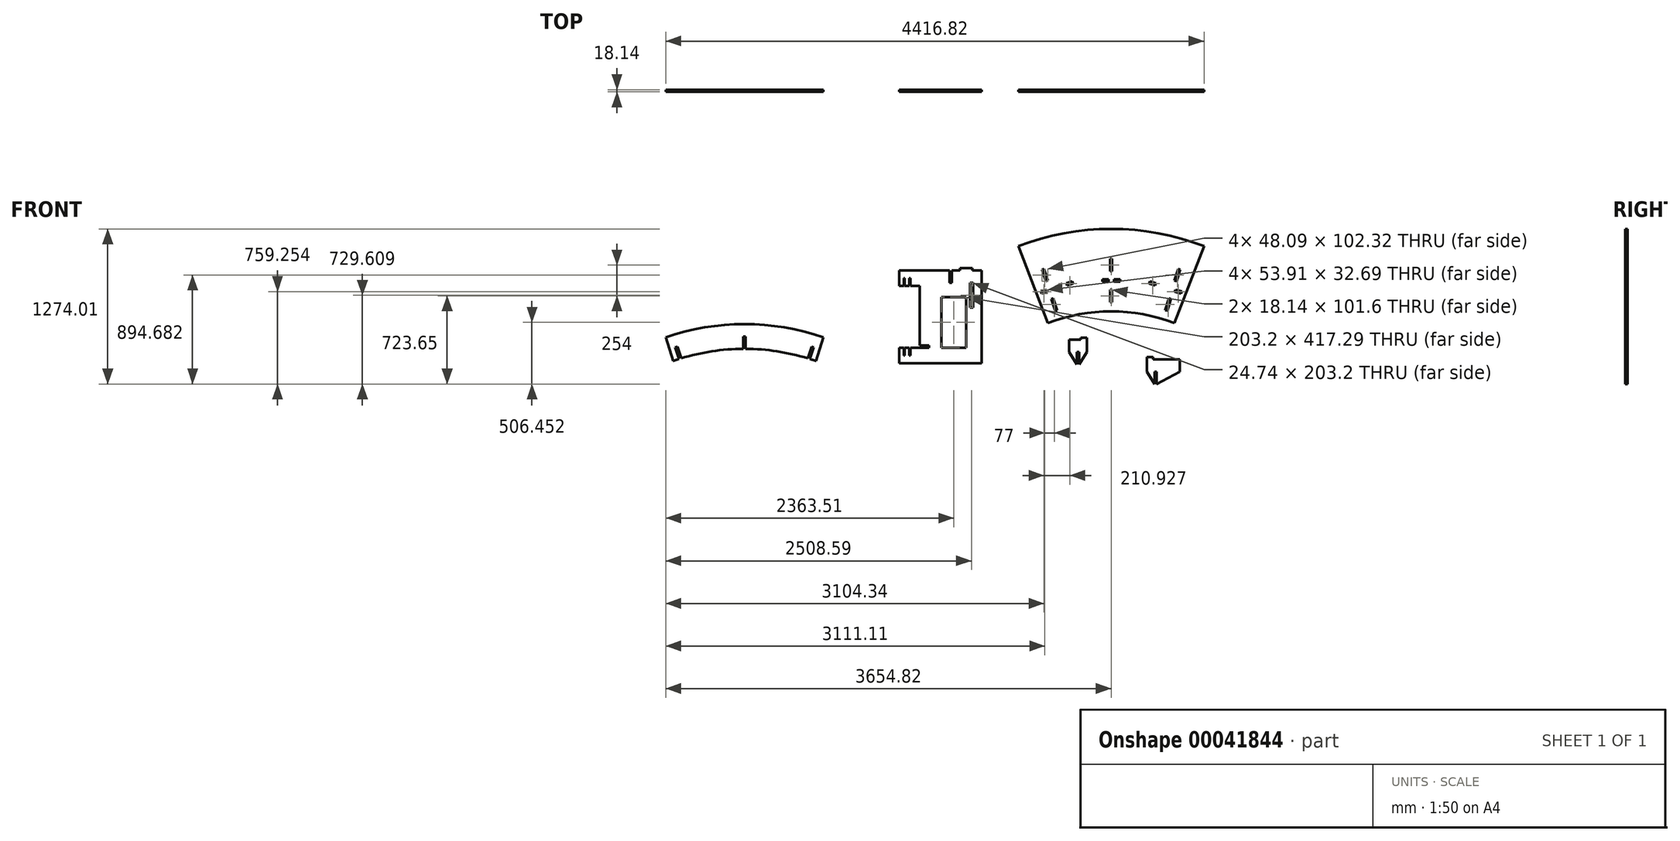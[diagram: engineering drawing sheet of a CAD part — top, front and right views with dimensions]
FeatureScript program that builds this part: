
annotation { "Feature Type Name" : "Feature", "Feature Type Description" : "" }
export const myFeature = defineFeature(function(context is Context, id is Id, definition is map)
    precondition{}
    {
        {
            var Q0;
            Q0=qCreatedBy(makeId("Front.planeOp"),FACE);
            var sketch = newSketch(context, id + "F0", { "sketchPlane" : qUnion([Q0])});
            skArc(sketch, "E0", {"start": v(822.71, 0) * mm, "mid": v(60.71, 141.8) * mm, "end": v(-701.29, 0) * mm});
            skArc(sketch, "E1.0", {"start": v(579.07, -632) * mm, "mid": v(60.71, -535.54) * mm, "end": v(-457.65, -632) * mm});
            skLineSegment(sketch, "E2", {"start": v(-701.29, 0) * mm, "end": v(-457.65, -632) * mm});
            skLineSegment(sketch, "E3", {"start": v(579.07, -632) * mm, "end": v(822.71, 0) * mm});
            skLineSegment(sketch, "E4.bottom", {"start": v(-1510, -199.4) * mm, "end": v(-1002, -199.4) * mm});
            skLineSegment(sketch, "E4.top", {"start": v(-1510, -961.4) * mm, "end": v(-1002, -961.4) * mm});
            skLineSegment(sketch, "E4.left", {"start": v(-1510, -326.4) * mm, "end": v(-1510, -815.86) * mm});
            skLineSegment(sketch, "E4.right", {"start": v(-1002, -199.4) * mm, "end": v(-1002, -961.4) * mm});
            skLineSegment(sketch, "E5.bottom", {"start": v(-1510, -199.4) * mm, "end": v(-1679.33, -199.4) * mm});
            skLineSegment(sketch, "E5.top", {"start": v(-1510, -326.4) * mm, "end": v(-1585.35, -326.4) * mm});
            skLineSegment(sketch, "E5.right", {"start": v(-1679.33, -199.4) * mm, "end": v(-1679.33, -326.4) * mm});
            skLineSegment(sketch, "E6", {"start": v(-1510, -580.4) * mm, "end": v(-1002, -580.4) * mm, "construction": true});
            skLineSegment(sketch, "E7", {"start": v(-1679.33, -262.9) * mm, "end": v(-1641.23, -262.9) * mm, "construction": true});
            skLineSegment(sketch, "E8.top", {"start": v(-1641.23, -262.9) * mm, "end": v(-1632.34, -262.9) * mm});
            skLineSegment(sketch, "E8.left", {"start": v(-1641.23, -326.4) * mm, "end": v(-1641.23, -262.9) * mm});
            skLineSegment(sketch, "E8.right", {"start": v(-1632.34, -326.4) * mm, "end": v(-1632.34, -262.9) * mm});
            skLineSegment(sketch, "E9", {"start": v(-1632.34, -262.9) * mm, "end": v(-1594.24, -262.9) * mm, "construction": true});
            skLineSegment(sketch, "E10.top", {"start": v(-1594.24, -262.9) * mm, "end": v(-1585.35, -262.9) * mm});
            skLineSegment(sketch, "E10.left", {"start": v(-1594.24, -326.4) * mm, "end": v(-1594.24, -262.9) * mm});
            skLineSegment(sketch, "E10.right", {"start": v(-1585.35, -326.4) * mm, "end": v(-1585.35, -262.9) * mm});
            skLineSegment(sketch, "E11.trimOffspring", {"start": v(-1641.23, -326.4) * mm, "end": v(-1679.33, -326.4) * mm});
            skLineSegment(sketch, "E12.trimOffspring", {"start": v(-1594.24, -326.4) * mm, "end": v(-1632.34, -326.4) * mm});
            skLineSegment(sketch, "E13.MirrorCS", {"start": v(-1641.23, -834.4) * mm, "end": v(-1679.33, -834.4) * mm});
            skLineSegment(sketch, "E14.MirrorCS", {"start": v(-1510, -834.4) * mm, "end": v(-1585.35, -834.4) * mm});
            skLineSegment(sketch, "E15.MirrorCS", {"start": v(-1632.34, -897.9) * mm, "end": v(-1594.24, -897.9) * mm, "construction": true});
            skLineSegment(sketch, "E16.MirrorCS", {"start": v(-1679.33, -897.9) * mm, "end": v(-1641.23, -897.9) * mm, "construction": true});
            skLineSegment(sketch, "E17.MirrorCS", {"start": v(-1594.24, -834.4) * mm, "end": v(-1594.24, -897.9) * mm});
            skLineSegment(sketch, "E18.MirrorCS", {"start": v(-1594.24, -834.4) * mm, "end": v(-1632.34, -834.4) * mm});
            skLineSegment(sketch, "E19.MirrorCS", {"start": v(-1679.33, -961.4) * mm, "end": v(-1679.33, -834.4) * mm});
            skLineSegment(sketch, "E20.MirrorCS", {"start": v(-1632.34, -834.4) * mm, "end": v(-1632.34, -897.9) * mm});
            skLineSegment(sketch, "E21.MirrorCS", {"start": v(-1641.23, -834.4) * mm, "end": v(-1641.23, -897.9) * mm});
            skLineSegment(sketch, "E22.MirrorCS", {"start": v(-1510, -961.4) * mm, "end": v(-1679.33, -961.4) * mm});
            skLineSegment(sketch, "E23.MirrorCS", {"start": v(-1641.23, -897.9) * mm, "end": v(-1632.34, -897.9) * mm});
            skLineSegment(sketch, "E24.MirrorCS", {"start": v(-1594.24, -897.9) * mm, "end": v(-1585.35, -897.9) * mm});
            skLineSegment(sketch, "E25.MirrorCS", {"start": v(-1585.35, -834.4) * mm, "end": v(-1585.35, -897.9) * mm});
            skLineSegment(sketch, "E26", {"start": v(-376.14, -603.35) * mm, "end": v(-581.47, 42.11) * mm, "construction": true});
            skLineSegment(sketch, "E27", {"start": v(60.71, -1976.58) * mm, "end": v(60.71, 636.15) * mm, "construction": true});
            skLineSegment(sketch, "E28", {"start": v(-476.24, -288.69) * mm, "end": v(-458.95, -283.19) * mm});
            skLineSegment(sketch, "E29", {"start": v(-458.95, -283.19) * mm, "end": v(-489.75, -186.37) * mm});
            skLineSegment(sketch, "E30", {"start": v(-489.75, -186.37) * mm, "end": v(-507.04, -191.87) * mm});
            skLineSegment(sketch, "E31", {"start": v(-507.04, -191.87) * mm, "end": v(-476.24, -288.69) * mm});
            skLineSegment(sketch, "E32.bottom", {"start": v(-1433.8, -199.4) * mm, "end": v(-1332.2, -199.4) * mm});
            skLineSegment(sketch, "E32.top", {"start": v(-1433.8, -181.26) * mm, "end": v(-1332.2, -181.26) * mm});
            skLineSegment(sketch, "E32.left", {"start": v(-1433.8, -199.4) * mm, "end": v(-1433.8, -181.26) * mm});
            skLineSegment(sketch, "E32.right", {"start": v(-1332.2, -199.4) * mm, "end": v(-1332.2, -181.26) * mm});
            skLineSegment(sketch, "E33", {"start": v(-1256, -199.4) * mm, "end": v(-1256, -961.4) * mm, "construction": true});
            skLineSegment(sketch, "E34.MirrorCS", {"start": v(-1078.2, -199.4) * mm, "end": v(-1078.2, -181.26) * mm});
            skLineSegment(sketch, "E35.MirrorCS", {"start": v(-1078.2, -199.4) * mm, "end": v(-1179.8, -199.4) * mm});
            skLineSegment(sketch, "E36.MirrorCS", {"start": v(-1179.8, -199.4) * mm, "end": v(-1179.8, -181.26) * mm});
            skLineSegment(sketch, "E37.MirrorCS", {"start": v(-1078.2, -181.26) * mm, "end": v(-1179.8, -181.26) * mm});
            skLineSegment(sketch, "E38.bottom", {"start": v(51.64, -103.76) * mm, "end": v(69.78, -103.76) * mm});
            skLineSegment(sketch, "E38.top", {"start": v(51.64, -205.36) * mm, "end": v(69.78, -205.36) * mm});
            skLineSegment(sketch, "E38.left", {"start": v(51.64, -103.76) * mm, "end": v(51.64, -205.36) * mm});
            skLineSegment(sketch, "E38.right", {"start": v(69.78, -103.76) * mm, "end": v(69.78, -205.36) * mm});
            skPoint(sketch, "E39", {"position": v(60.71, -103.76) * mm});
            skLineSegment(sketch, "E40", {"start": v(51.71, -281.56) * mm, "end": v(78.37, -281.56) * mm, "construction": true});
            skPoint(sketch, "E41.MirrorP", {"position": v(60.71, -459.36) * mm});
            skLineSegment(sketch, "E42.MirrorCS", {"start": v(51.64, -459.36) * mm, "end": v(69.78, -459.36) * mm});
            skLineSegment(sketch, "E43.MirrorCS", {"start": v(51.64, -459.36) * mm, "end": v(51.64, -357.76) * mm});
            skLineSegment(sketch, "E44.MirrorCS", {"start": v(51.64, -357.76) * mm, "end": v(69.78, -357.76) * mm});
            skLineSegment(sketch, "E45.MirrorCS", {"start": v(69.78, -459.36) * mm, "end": v(69.78, -357.76) * mm});
            skPoint(sketch, "E46", {"position": v(61.08, -535.54) * mm});
            skPoint(sketch, "E47", {"position": v(61.08, 141.8) * mm});
            skLineSegment(sketch, "E48.bottom", {"start": v(-283.81, -768.8) * mm, "end": v(-138.67, -768.8) * mm});
            skLineSegment(sketch, "E48.left", {"start": v(-283.81, -768.8) * mm, "end": v(-283.81, -870.4) * mm});
            skLineSegment(sketch, "E49.left", {"start": v(-220.31, -870.4) * mm, "end": v(-220.31, -972) * mm});
            skLineSegment(sketch, "E49.right", {"start": v(-202.17, -870.4) * mm, "end": v(-202.17, -972) * mm});
            skPoint(sketch, "E50", {"position": v(-211.24, -870.4) * mm});
            skLineSegment(sketch, "E49.bottom", {"start": v(-220.31, -870.4) * mm, "end": v(-202.17, -870.4) * mm});
            skLineSegment(sketch, "E51", {"start": v(-283.81, -870.4) * mm, "end": v(-220.31, -972) * mm});
            skLineSegment(sketch, "E52.left", {"start": v(-1265.07, -199.4) * mm, "end": v(-1265.07, -301) * mm});
            skPoint(sketch, "E53", {"position": v(-1256, -301) * mm});
            skLineSegment(sketch, "E52.right", {"start": v(-1246.92, -199.4) * mm, "end": v(-1246.92, -301) * mm});
            skPoint(sketch, "E54", {"position": v(-1256, -199.4) * mm});
            skLineSegment(sketch, "E52.bottom", {"start": v(-1265.07, -199.4) * mm, "end": v(-1246.92, -199.4) * mm});
            skLineSegment(sketch, "E52.top", {"start": v(-1265.07, -301) * mm, "end": v(-1246.92, -301) * mm});
            skPoint(sketch, "E55.orphan", {"position": v(-283.81, -972) * mm});
            skPoint(sketch, "E56.orphan", {"position": v(-84.24, -972) * mm});
            skLineSegment(sketch, "E57", {"start": v(-211.24, -870.4) * mm, "end": v(-211.24, -744.65) * mm, "construction": true});
            skLineSegment(sketch, "E58.MirrorCS", {"start": v(-138.67, -768.8) * mm, "end": v(-138.67, -870.4) * mm});
            skLineSegment(sketch, "E59.MirrorCS", {"start": v(-138.67, -870.4) * mm, "end": v(-202.17, -972) * mm});
            skLineSegment(sketch, "E60.bottom", {"start": v(-283.81, -768.8) * mm, "end": v(-233.01, -768.8) * mm});
            skLineSegment(sketch, "E60.top", {"start": v(-283.81, -750.67) * mm, "end": v(-233.01, -750.67) * mm});
            skLineSegment(sketch, "E60.left", {"start": v(-283.81, -768.8) * mm, "end": v(-283.81, -750.67) * mm});
            skLineSegment(sketch, "E60.right", {"start": v(-233.01, -768.8) * mm, "end": v(-233.01, -750.67) * mm});
            skLineSegment(sketch, "E61.MirrorCS", {"start": v(-189.47, -768.8) * mm, "end": v(-189.47, -750.67) * mm});
            skLineSegment(sketch, "E62.MirrorCS", {"start": v(-138.67, -768.8) * mm, "end": v(-138.67, -750.67) * mm});
            skLineSegment(sketch, "E63.MirrorCS", {"start": v(-138.67, -768.8) * mm, "end": v(-189.47, -768.8) * mm});
            skLineSegment(sketch, "E64.MirrorCS", {"start": v(-138.67, -750.67) * mm, "end": v(-189.47, -750.67) * mm});
            skLineSegment(sketch, "E65", {"start": v(-516.73, -372.01) * mm, "end": v(-511.23, -389.3) * mm});
            skPoint(sketch, "E66.positionSnap0", {"position": v(-513.98, -380.66) * mm});
            skLineSegment(sketch, "E67", {"start": v(-516.73, -372.01) * mm, "end": v(-468.32, -356.61) * mm});
            skLineSegment(sketch, "E68", {"start": v(-511.23, -389.3) * mm, "end": v(-462.82, -373.9) * mm});
            skLineSegment(sketch, "E69", {"start": v(-468.32, -356.61) * mm, "end": v(-462.82, -373.9) * mm});
            skPoint(sketch, "E70", {"position": v(60.79, -132.27) * mm});
            skLineSegment(sketch, "E71", {"start": v(-233.01, -759.74) * mm, "end": v(-189.47, -759.74) * mm, "construction": true});
            skPoint(sketch, "E72", {"position": v(-211.24, -759.74) * mm});
            skLineSegment(sketch, "E73.left", {"start": v(-11.86, -290.63) * mm, "end": v(-11.86, -272.49) * mm});
            skLineSegment(sketch, "E73.bottom", {"start": v(-11.86, -290.63) * mm, "end": v(38.94, -290.63) * mm});
            skLineSegment(sketch, "E73.top", {"start": v(-11.86, -272.49) * mm, "end": v(38.94, -272.49) * mm});
            skLineSegment(sketch, "E73.right", {"start": v(38.94, -290.63) * mm, "end": v(38.94, -272.49) * mm});
            skLineSegment(sketch, "E74.MirrorCS", {"start": v(133.28, -290.63) * mm, "end": v(133.28, -272.49) * mm});
            skLineSegment(sketch, "E75.MirrorCS", {"start": v(133.28, -290.63) * mm, "end": v(82.48, -290.63) * mm});
            skLineSegment(sketch, "E76.MirrorCS", {"start": v(82.48, -290.63) * mm, "end": v(82.48, -272.49) * mm});
            skLineSegment(sketch, "E77.MirrorCS", {"start": v(133.28, -272.49) * mm, "end": v(82.48, -272.49) * mm});
            skPoint(sketch, "E78", {"position": v(38.94, -281.56) * mm});
            skLineSegment(sketch, "E79", {"start": v(38.94, -281.56) * mm, "end": v(51.71, -281.56) * mm, "construction": true});
            skLineSegment(sketch, "E80", {"start": v(-465.57, -365.26) * mm, "end": v(-303.05, -313.56) * mm, "construction": true});
            skLineSegment(sketch, "E81.MirrorCS", {"start": v(-430.04, -433.92) * mm, "end": v(-412.75, -428.42) * mm});
            skLineSegment(sketch, "E82.MirrorCS", {"start": v(-381.95, -525.24) * mm, "end": v(-399.24, -530.74) * mm});
            skLineSegment(sketch, "E83.MirrorCS", {"start": v(-399.24, -530.74) * mm, "end": v(-430.04, -433.92) * mm});
            skLineSegment(sketch, "E84.MirrorCS", {"start": v(-412.75, -428.42) * mm, "end": v(-381.95, -525.24) * mm});
            skLineSegment(sketch, "E85.MirrorCS", {"start": v(597.66, -288.69) * mm, "end": v(580.37, -283.19) * mm});
            skLineSegment(sketch, "E86.MirrorCS", {"start": v(611.17, -186.37) * mm, "end": v(628.46, -191.87) * mm});
            skLineSegment(sketch, "E87.MirrorCS", {"start": v(580.37, -283.19) * mm, "end": v(611.17, -186.37) * mm});
            skLineSegment(sketch, "E88.MirrorCS", {"start": v(628.46, -191.87) * mm, "end": v(597.66, -288.69) * mm});
            skLineSegment(sketch, "E89.MirrorCS", {"start": v(551.46, -433.92) * mm, "end": v(534.17, -428.42) * mm});
            skLineSegment(sketch, "E90.MirrorCS", {"start": v(503.37, -525.24) * mm, "end": v(520.66, -530.74) * mm});
            skLineSegment(sketch, "E91.MirrorCS", {"start": v(520.66, -530.74) * mm, "end": v(551.46, -433.92) * mm});
            skLineSegment(sketch, "E92.MirrorCS", {"start": v(534.17, -428.42) * mm, "end": v(503.37, -525.24) * mm});
            skLineSegment(sketch, "E93.MirrorCS", {"start": v(638.15, -372.01) * mm, "end": v(632.65, -389.3) * mm});
            skLineSegment(sketch, "E94.MirrorCS", {"start": v(589.74, -356.61) * mm, "end": v(584.24, -373.9) * mm});
            skPoint(sketch, "E95.MirrorP", {"position": v(635.4, -380.66) * mm});
            skLineSegment(sketch, "E96.MirrorCS", {"start": v(632.65, -389.3) * mm, "end": v(584.24, -373.9) * mm});
            skLineSegment(sketch, "E97.MirrorCS", {"start": v(638.15, -372.01) * mm, "end": v(589.74, -356.61) * mm});
            skLineSegment(sketch, "E98", {"start": v(-384.31, -339.4) * mm, "end": v(-444.42, -150.46) * mm, "construction": true});
            skPoint(sketch, "E99.MirrorP", {"position": v(-254.64, -298.16) * mm});
            skLineSegment(sketch, "E100.MirrorCS", {"start": v(-305.8, -304.91) * mm, "end": v(-300.3, -322.2) * mm});
            skLineSegment(sketch, "E101.MirrorCS", {"start": v(-257.4, -289.51) * mm, "end": v(-251.9, -306.8) * mm});
            skLineSegment(sketch, "E102.MirrorCS", {"start": v(-257.4, -289.51) * mm, "end": v(-305.8, -304.91) * mm});
            skLineSegment(sketch, "E103.MirrorCS", {"start": v(-251.9, -306.8) * mm, "end": v(-300.3, -322.2) * mm});
            skLineSegment(sketch, "E104.MirrorCS", {"start": v(378.81, -289.51) * mm, "end": v(373.31, -306.8) * mm});
            skPoint(sketch, "E105.MirrorP", {"position": v(376.06, -298.16) * mm});
            skLineSegment(sketch, "E106.MirrorCS", {"start": v(373.31, -306.8) * mm, "end": v(421.72, -322.2) * mm});
            skLineSegment(sketch, "E107.MirrorCS", {"start": v(427.22, -304.91) * mm, "end": v(421.72, -322.2) * mm});
            skLineSegment(sketch, "E108.MirrorCS", {"start": v(378.81, -289.51) * mm, "end": v(427.22, -304.91) * mm});
            skLineSegment(sketch, "E109", {"start": v(-1299.86, -199.4) * mm, "end": v(-1299.86, -417.12) * mm, "construction": true});
            skLineSegment(sketch, "E110", {"start": v(-1002, -510.07) * mm, "end": v(-1129, -510.07) * mm, "construction": true});
            skLineSegment(sketch, "E111", {"start": v(-1319.66, -961.4) * mm, "end": v(-1319.66, -834.4) * mm, "construction": true});
            skLineSegment(sketch, "E112.bottom", {"start": v(-1332.2, -417.12) * mm, "end": v(-1129, -417.12) * mm});
            skLineSegment(sketch, "E112.top", {"start": v(-1332.2, -834.4) * mm, "end": v(-1129, -834.4) * mm});
            skLineSegment(sketch, "E112.left", {"start": v(-1332.2, -417.12) * mm, "end": v(-1332.2, -834.4) * mm});
            skLineSegment(sketch, "E112.right", {"start": v(-1129, -417.12) * mm, "end": v(-1129, -834.4) * mm});
            skLineSegment(sketch, "E113.left", {"start": v(-1332.2, -834.4) * mm, "end": v(-1332.2, -815.86) * mm});
            skLineSegment(sketch, "E113.right", {"start": v(-1433.8, -834.4) * mm, "end": v(-1433.8, -815.86) * mm});
            skPoint(sketch, "E114", {"position": v(489.26, -919.94) * mm});
            skLineSegment(sketch, "E115.bottom", {"start": v(353.19, -929) * mm, "end": v(625.33, -929) * mm});
            skPoint(sketch, "E116", {"position": v(425.76, -1030.6) * mm});
            skLineSegment(sketch, "E115.left", {"start": v(353.19, -929) * mm, "end": v(353.19, -1030.6) * mm});
            skLineSegment(sketch, "E117.MirrorCS", {"start": v(625.33, -929) * mm, "end": v(574.53, -929) * mm});
            skLineSegment(sketch, "E118.right", {"start": v(434.83, -1030.6) * mm, "end": v(434.83, -1132.2) * mm});
            skLineSegment(sketch, "E118.left", {"start": v(416.69, -1030.6) * mm, "end": v(416.69, -1132.2) * mm});
            skPoint(sketch, "E119.orphan", {"position": v(514.52, -1119.3) * mm});
            skLineSegment(sketch, "E120.MirrorCS", {"start": v(625.33, -910.87) * mm, "end": v(574.53, -910.87) * mm});
            skLineSegment(sketch, "E121.MirrorCS", {"start": v(625.33, -929) * mm, "end": v(625.33, -1030.6) * mm});
            skLineSegment(sketch, "E122", {"start": v(353.19, -1030.6) * mm, "end": v(416.69, -1132.2) * mm});
            skLineSegment(sketch, "E123.top", {"start": v(353.19, -910.87) * mm, "end": v(403.99, -910.87) * mm});
            skPoint(sketch, "E124.orphan", {"position": v(353.19, -1119.3) * mm});
            skLineSegment(sketch, "E125.MirrorCS", {"start": v(625.33, -1030.6) * mm, "end": v(434.83, -1132.2) * mm});
            skLineSegment(sketch, "E123.bottom", {"start": v(353.19, -929) * mm, "end": v(403.99, -929) * mm});
            skLineSegment(sketch, "E126", {"start": v(403.99, -919.94) * mm, "end": v(574.53, -919.94) * mm, "construction": true});
            skLineSegment(sketch, "E123.right", {"start": v(403.99, -929) * mm, "end": v(403.99, -910.87) * mm});
            skLineSegment(sketch, "E127.MirrorCS", {"start": v(574.53, -929) * mm, "end": v(574.53, -910.87) * mm});
            skLineSegment(sketch, "E118.bottom", {"start": v(416.69, -1030.6) * mm, "end": v(434.83, -1030.6) * mm});
            skLineSegment(sketch, "E123.left", {"start": v(353.19, -929) * mm, "end": v(353.19, -910.87) * mm});
            skLineSegment(sketch, "E128.MirrorCS", {"start": v(625.33, -929) * mm, "end": v(625.33, -910.87) * mm});
            skLineSegment(sketch, "E129.MirrorCS", {"start": v(1775.37, -902.65) * mm, "end": v(1775.39, -902.65) * mm});
            skLineSegment(sketch, "E130", {"start": v(-1433.8, -815.86) * mm, "end": v(-1510, -815.86) * mm});
            skLineSegment(sketch, "E131", {"start": v(-1433.8, -834.4) * mm, "end": v(-1510, -834.4) * mm});
            skPoint(sketch, "E132", {"position": v(-2969.11, -919.18) * mm});
            skPoint(sketch, "E133", {"position": v(-2947.27, -769.9) * mm});
            skPoint(sketch, "E134", {"position": v(-2947.34, -741.38) * mm});
            skLineSegment(sketch, "E135.right", {"start": v(-2938.27, -741.38) * mm, "end": v(-2938.27, -842.98) * mm});
            skLineSegment(sketch, "E135.left", {"start": v(-2956.41, -741.38) * mm, "end": v(-2956.41, -842.98) * mm});
            skLineSegment(sketch, "E136", {"start": v(-3497.8, -824) * mm, "end": v(-3515.1, -829.5) * mm});
            skLineSegment(sketch, "E137.MirrorCS", {"start": v(-2396.88, -824) * mm, "end": v(-2379.6, -829.5) * mm});
            skLineSegment(sketch, "E135.top", {"start": v(-2956.41, -842.98) * mm, "end": v(-2956.16, -842.98) * mm});
            skLineSegment(sketch, "E135.bottom", {"start": v(-2956.41, -741.38) * mm, "end": v(-2938.27, -741.38) * mm});
            skLineSegment(sketch, "E138", {"start": v(-3515.1, -829.5) * mm, "end": v(-3484.3, -926.31) * mm});
            skLineSegment(sketch, "E139", {"start": v(-3467, -920.81) * mm, "end": v(-3497.8, -824) * mm});
            skLineSegment(sketch, "E140.MirrorCS", {"start": v(-2379.6, -829.5) * mm, "end": v(-2410.4, -926.31) * mm});
            skLineSegment(sketch, "E141.MirrorCS", {"start": v(-2427.68, -920.81) * mm, "end": v(-2396.88, -824) * mm});
            skArc(sketch, "E142.0", {"start": v(-2300.58, -748.7) * mm, "mid": v(-2947.34, -639.76) * mm, "end": v(-3594.1, -748.7) * mm});
            skArc(sketch, "E143.0", {"start": v(-2362.2, -942.4) * mm, "mid": v(-2386.24, -934.18) * mm, "end": v(-2410.4, -926.31) * mm});
            skArc(sketch, "E144.trimOffspring", {"start": v(-2956.16, -842.98) * mm, "mid": v(-3214.43, -863.21) * mm, "end": v(-3466.98, -920.9) * mm});
            skLineSegment(sketch, "E145.trimOffspring", {"start": v(-2938.52, -842.98) * mm, "end": v(-2938.27, -842.98) * mm});
            skLineSegment(sketch, "E146", {"start": v(-3467, -920.81) * mm, "end": v(-3466.98, -920.9) * mm});
            skLineSegment(sketch, "E147", {"start": v(-2427.68, -920.81) * mm, "end": v(-2427.7, -920.9) * mm});
            skArc(sketch, "E148.trimOffspring", {"start": v(-2427.7, -920.9) * mm, "mid": v(-2680.26, -863.21) * mm, "end": v(-2938.52, -842.98) * mm});
            skArc(sketch, "E149.trimOffspring", {"start": v(-3484.3, -926.31) * mm, "mid": v(-3508.45, -934.18) * mm, "end": v(-3532.48, -942.4) * mm});
            skLineSegment(sketch, "E150", {"start": v(-3532.48, -942.4) * mm, "end": v(-3594.1, -748.7) * mm});
            skLineSegment(sketch, "E151", {"start": v(-2947.27, -769.9) * mm, "end": v(-2947.34, -741.38) * mm, "construction": true});
            skLineSegment(sketch, "E152.0", {"start": v(-2331.18, -844.9) * mm, "end": v(-2361.98, -941.71) * mm});
            skLineSegment(sketch, "E153", {"start": v(-2361.98, -941.71) * mm, "end": v(-2362.2, -942.4) * mm});
            skLineSegment(sketch, "E154", {"start": v(-2331.18, -844.9) * mm, "end": v(-2300.58, -748.7) * mm});
            skLineSegment(sketch, "E155", {"start": v(-840.28, 210.13) * mm, "end": v(-840.5, 209.44) * mm});
            skLineSegment(sketch, "E156", {"start": v(998.97, -483.8) * mm, "end": v(2014.97, -483.8) * mm, "construction": true});
            skLineSegment(sketch, "E157.0", {"start": v(998.97, -501.96) * mm, "end": v(2014.97, -501.96) * mm, "construction": true});
            skLineSegment(sketch, "E158", {"start": v(998.97, -483.8) * mm, "end": v(998.97, -501.96) * mm, "construction": true});
            skLineSegment(sketch, "E159", {"start": v(2014.97, -483.8) * mm, "end": v(2014.97, -501.96) * mm, "construction": true});
            skLineSegment(sketch, "E160.0", {"start": v(-1073.15, -301) * mm, "end": v(-1073.15, -504.2) * mm});
            skPoint(sketch, "E161", {"position": v(-397.71, -535.54) * mm});
            skLineSegment(sketch, "E162.0", {"start": v(-1097.9, -301) * mm, "end": v(-1097.9, -504.2) * mm});
            skLineSegment(sketch, "E163", {"start": v(-1073.15, -504.2) * mm, "end": v(-1097.9, -504.2) * mm});
            skLineSegment(sketch, "E164.0", {"start": v(-1073.15, -301) * mm, "end": v(-1097.9, -301) * mm});
            skSolve(sketch);
        }
        {
            var Q0;
            Q0=makeQuery(id+"F0.imprint","IMPRINT",FACE,{"disambiguationData":[TD([[makeQuery(id+"F0.imprint","IMPRINT",EDGE,{"derivedFrom":sQuery(id+"F0.wireOp",EDGE,"E4.top")}),1.0]])]});
            var Q1;
            Q1=makeQuery(id+"F0.imprint","IMPRINT",FACE,{"disambiguationData":[TD([[makeQuery(id+"F0.imprint","IMPRINT",EDGE,{"derivedFrom":sQuery(id+"F0.wireOp",EDGE,"E32.bottom")}),1.0]])]});
            var Q2;
            Q2=makeQuery(id+"F0.imprint","IMPRINT",FACE,{"disambiguationData":[TD([[makeQuery(id+"F0.imprint","IMPRINT",EDGE,{"derivedFrom":sQuery(id+"F0.wireOp",EDGE,"E34.MirrorCS")}),1.0]])]});
            var Q3;
            Q3=makeQuery(id+"F0.imprint","IMPRINT",FACE,{"disambiguationData":[TD([[makeQuery(id+"F0.imprint","IMPRINT",EDGE,{"derivedFrom":sQuery(id+"F0.wireOp",EDGE,"E48.bottom")}),-1.0]])]});
            var Q4;
            Q4=makeQuery(id+"F0.imprint","IMPRINT",FACE,{"disambiguationData":[TD([[makeQuery(id+"F0.imprint","IMPRINT",EDGE,{"derivedFrom":sQuery(id+"F0.wireOp",EDGE,"E61.MirrorCS")}),-1.0]])]});
            var Q5;
            Q5=makeQuery(id+"F0.imprint","IMPRINT",FACE,{"disambiguationData":[TD([[makeQuery(id+"F0.imprint","IMPRINT",EDGE,{"derivedFrom":sQuery(id+"F0.wireOp",EDGE,"E60.bottom")}),1.0]])]});
            var Q6;
            Q6=makeQuery(id+"F0.imprint","IMPRINT",FACE,{"disambiguationData":[TD([[makeQuery(id+"F0.imprint","IMPRINT",EDGE,{"derivedFrom":sQuery(id+"F0.wireOp",EDGE,"E0")}),1.0]])]});
            var Q7;
            Q7=makeQuery(id+"F0.imprint","IMPRINT",FACE,{"disambiguationData":[TD([[makeQuery(id+"F0.imprint","IMPRINT",EDGE,{"derivedFrom":sQuery(id+"F0.wireOp",EDGE,"E123.top")}),-1.0]])]});
            var Q8;
            Q8=makeQuery(id+"F0.imprint","IMPRINT",FACE,{"disambiguationData":[TD([[makeQuery(id+"F0.imprint","IMPRINT",EDGE,{"derivedFrom":sQuery(id+"F0.wireOp",EDGE,"E115.bottom")}),-1.0]])]});
            var Q9;
            Q9=makeQuery(id+"F0.imprint","IMPRINT",FACE,{"disambiguationData":[TD([[makeQuery(id+"F0.imprint","IMPRINT",EDGE,{"derivedFrom":sQuery(id+"F0.wireOp",EDGE,"E117.MirrorCS")}),-1.0]])]});
            var Q10;
            {var subQ11=sQuery(id+"F0.wireOp",EDGE,"4b4208f6-c2fb-4491-82b5-bbb72651a30f");Q10=makeQuery(id+"F0.imprint","IMPRINT",FACE,{"disambiguationData":[TD([[makeQuery(id+"F0.imprint","IMPRINT",EDGE,{"derivedFrom":subQ11}),1.0]])]});}
            var Q11;
            Q11=makeQuery(id+"F0.imprint","IMPRINT",FACE,{"disambiguationData":[TD([[makeQuery(id+"F0.imprint","IMPRINT",EDGE,{"derivedFrom":sQuery(id+"F0.wireOp",EDGE,"ZEEkujvX-f0nl-X2ht-5uEe-wjA7yF6qMzgc")}),1.0]])]});
            var Q12;
            {var subQ0=sQuery(id+"F0.wireOp",EDGE,"cHDWE3Ce-WObb-T2iv-pb7J-tTBgFW9YY9rB");Q12=makeQuery(id+"F0.imprint","IMPRINT",FACE,{"disambiguationData":[TD([[makeQuery(id+"F0.imprint","IMPRINT",EDGE,{"derivedFrom":subQ0}),-1.0]])]});}
            var Q13;
            Q13=makeQuery(id+"F0.imprint","IMPRINT",FACE,{"disambiguationData":[TD([[makeQuery(id+"F0.imprint","IMPRINT",EDGE,{"derivedFrom":sQuery(id+"F0.wireOp",EDGE,"80414a30-6be5-4261-b871-3fd237e30337.0")}),1.0]])]});
            var Q14;
            Q14=makeQuery(id+"F0.imprint","IMPRINT",FACE,{"disambiguationData":[TD([[makeQuery(id+"F0.imprint","IMPRINT",EDGE,{"derivedFrom":sQuery(id+"F0.wireOp",EDGE,"E135.right")}),1.0]])]});
            var Q15;
            {var subQ4=sQuery(id+"F0.wireOp",EDGE,"E4.right");Q15=makeQuery(id+"F0.imprint","IMPRINT",FACE,{"disambiguationData":[TD([[makeQuery(id+"F0.imprint","IMPRINT",EDGE,{"derivedFrom":subQ4}),-1.0]])]});}
            var Q16;
            {var subQ0=sQuery(id+"F0.wireOp",EDGE,"E12.trimOffspring");Q16=makeQuery(id+"F0.imprint","IMPRINT",FACE,{"disambiguationData":[TD([[makeQuery(id+"F0.imprint","IMPRINT",EDGE,{"derivedFrom":subQ0}),-1.0]])]});}
            var Q17;
            {var subQ0=sQuery(id+"F0.wireOp",EDGE,"E11.trimOffspring");Q17=makeQuery(id+"F0.imprint","IMPRINT",FACE,{"disambiguationData":[TD([[makeQuery(id+"F0.imprint","IMPRINT",EDGE,{"derivedFrom":subQ0}),-1.0]])]});}
            extrude(context, id + "F1", {"entities" : qUnion([Q0, Q1, Q2, Q3, Q4, Q5, Q6, Q7, Q8, Q9, Q10, Q11, Q12, Q13, Q14, Q15, Q16, Q17]), "depth" : 18.14 * mm});
        }
    });
